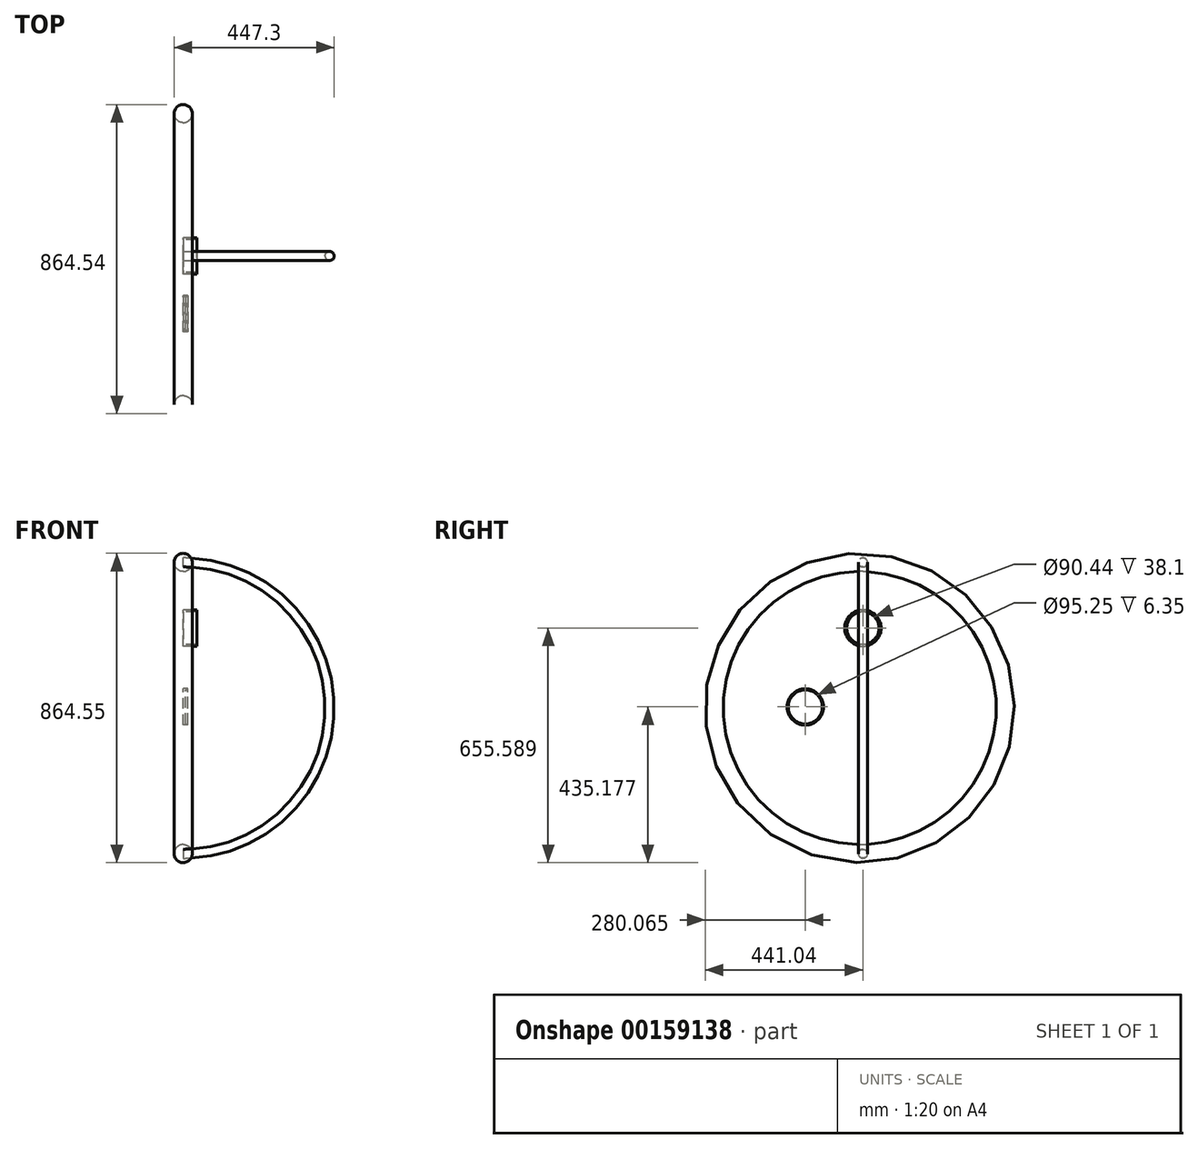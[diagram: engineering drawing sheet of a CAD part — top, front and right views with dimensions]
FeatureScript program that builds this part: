
annotation { "Feature Type Name" : "Feature", "Feature Type Description" : "" }
export const myFeature = defineFeature(function(context is Context, id is Id, definition is map)
    precondition{}
    {
        {
            var Q0;
            Q0=qCreatedBy(makeId("Front.planeOp"),FACE);
            var sketch = newSketch(context, id + "F0", { "sketchPlane" : qUnion([Q0])});
            skCircle(sketch, "E0", {"center": v(0, 0) * mm, "radius": 25.4 * mm});
            skSolve(sketch);
        }
        {
            var Q0;
            Q0=qCreatedBy(makeId("Right.planeOp"),FACE);
            var sketch = newSketch(context, id + "F1", { "sketchPlane" : qUnion([Q0])});
            skCircle(sketch, "E1", {"center": v(-8.77, -406.78) * mm, "radius": 406.88 * mm});
            skPoint(sketch, "E1.first.point", {"position": v(0, 0) * mm});
            skPoint(sketch, "E1.second.point", {"position": v(0, -813.57) * mm});
            skPoint(sketch, "E1.third.point", {"position": v(376.56, -276.11) * mm});
            skSolve(sketch);
        }
        {
            var Q0;
            Q0=makeQuery(id+"F0.imprint","IMPRINT",FACE,{"disambiguationData":[TD([[makeQuery(id+"F0.imprint","IMPRINT",EDGE,{"derivedFrom":sQuery(id+"F0.wireOp",EDGE,"E0")}),1.0]])]});
            var Q1;
            Q1=sQuery(id+"F1.wireOp",EDGE,"E1");
            sweep(context, id + "F2", {"profiles" : qUnion([Q0]), "path" : qUnion([Q1])});
        }
        {
            var Q0;
            Q0=qCreatedBy(makeId("Right.planeOp"),FACE);
            var sketch = newSketch(context, id + "F3", { "sketchPlane" : qUnion([Q0])});
            skCircle(sketch, "E2", {"center": v(0, 0) * mm, "radius": 12.7 * mm});
            skSolve(sketch);
        }
        {
            var Q0;
            Q0=qCreatedBy(makeId("Front.planeOp"),FACE);
            var sketch = newSketch(context, id + "F4", { "sketchPlane" : qUnion([Q0])});
            skArc(sketch, "E3", {"start": v(0, -814.12) * mm, "mid": v(409.2, -407.06) * mm, "end": v(0, 0) * mm});
            skSolve(sketch);
        }
        {
            var Q0;
            Q0=makeQuery(id+"F3.imprint","IMPRINT",FACE,{"disambiguationData":[TD([[makeQuery(id+"F3.imprint","IMPRINT",EDGE,{"derivedFrom":sQuery(id+"F3.wireOp",EDGE,"E2")}),1.0]])]});
            var Q1;
            Q1=sQuery(id+"F4.wireOp",EDGE,"E3");
            sweep(context, id + "F5", {"profiles" : qUnion([Q0]), "path" : qUnion([Q1])});
        }
        {
            var Q0;
            Q0=qCreatedBy(makeId("Right.planeOp"),FACE);
            var sketch = newSketch(context, id + "F6", { "sketchPlane" : qUnion([Q0])});
            skCircle(sketch, "E4", {"center": v(0, -183.47) * mm, "radius": 50.8 * mm});
            skSolve(sketch);
        }
        {
            var Q0;
            Q0 = qSketchRegion(id + "F6", true);
            extrude(context, id + "F7", {"entities" : qUnion([Q0]), "depth" : 38.1 * mm});
        }
        {
            var Q0;
            Q0=makeQuery(id+"F7.opExtrude","CAP_FACE",FACE,{"disambiguationData":[OSD([sQuery(id+"F6.wireOp",EDGE,"E4")])],"isStart":true});
            var sketch = newSketch(context, id + "F8", { "sketchPlane" : qUnion([Q0])});
            skCircle(sketch, "E5", {"center": v(0, -183.47) * mm, "radius": 45.22 * mm});
            skSolve(sketch);
        }
        {
            var Q0;
            Q0=makeQuery(id+"F8.imprint","IMPRINT",FACE,{"disambiguationData":[TD([[makeQuery(id+"F8.imprint","IMPRINT",EDGE,{"derivedFrom":sQuery(id+"F8.wireOp",EDGE,"E5")}),1.0]])]});
            extrude(context, id + "F9", {"entities" : qUnion([Q0]), "operationType" : NewBodyOperationType.REMOVE, "oppositeDirection" : true, "depth" : 50.8 * mm});
        }
        {
            var Q0;
            Q0=qCreatedBy(makeId("Right.planeOp"),FACE);
            var sketch = newSketch(context, id + "F10", { "sketchPlane" : qUnion([Q0])});
            skCircle(sketch, "E6", {"center": v(-160.98, -403.88) * mm, "radius": 50.8 * mm});
            skSolve(sketch);
        }
        {
            var Q0;
            Q0 = qSketchRegion(id + "F10", true);
            extrude(context, id + "F11", {"entities" : qUnion([Q0]), "depth" : 12.7 * mm});
        }
        {
            var Q0;
            Q0=makeQuery(id+"F11.opExtrude","CAP_FACE",FACE,{"disambiguationData":[OSD([sQuery(id+"F10.wireOp",EDGE,"E6")])],"isStart":false});
            var sketch = newSketch(context, id + "F12", { "sketchPlane" : qUnion([Q0])});
            skCircle(sketch, "E7", {"center": v(-160.98, -403.88) * mm, "radius": 47.63 * mm});
            skSolve(sketch);
        }
        {
            var Q0;
            Q0=makeQuery(id+"F12.imprint","IMPRINT",FACE,{"disambiguationData":[TD([[makeQuery(id+"F12.imprint","IMPRINT",EDGE,{"derivedFrom":sQuery(id+"F12.wireOp",EDGE,"E7")}),1.0]])]});
            extrude(context, id + "F13", {"entities" : qUnion([Q0]), "operationType" : NewBodyOperationType.REMOVE, "oppositeDirection" : true, "depth" : 6.35 * mm});
        }
    });
